# Revit family: RRHS
name_source: partatom
category: Generic Models
revit_build: Autodesk Revit 2018 (Build: 20190510_1515(x64)
units: mm (PartAtom-declared; Revit-internal decimal feet)

## family parameters
Always vertical = No
Can host rebar = No
Cut with Voids When Loaded = No
Part Type = Normal
Room Calculation Point = No
Round Connector Dimension = Use Diameter
Shared = Yes
Work Plane-Based = Yes

## types (7) — shared parameters
Default Elevation = 48 "
Spacer Material = <By Category>

## per-type parameters (varying)
| type | Description | Inside Diameter | Inside Radius | Length |
| RRHS5161 | Spacer Hygienic 304 5/16 Inch Hole Dia 1 Inch long | 0.313 " | 0.157 " | 1 " |
| RRHS5162 | Spacer Hygienic 304 5/16 Inch Hole Dia 2 Inch long | 0.313 " | 0.157 " | 2 " |
| RRHS5164 | Spacer Hygenic 304 5/16 Inch Hole Dia 4 Inch long | 0.313 " | 0.157 " | 4 " |
| RRHS7162 | Spacer Hygenic 304 7/16 Inch Hole Dia 2 Inch long | 0.438 " | 0.219 " | 2 " |
| RRHS7164 | Spacer Hygenic 304 7/16 Inch Hole Dia 4 Inch long | 0.438 " | 0.219 " | 4 " |
| RRHS7161 | Spacer Hygenic 304 7/16 Inch Hole Dia 1 Inch long | 0.438 " | 0.219 " | 1 " |
| RRHS9162 | Spacer Hygienic 304 9/16 Inch Hole Dia 2 Inch long | 0.563 " | 0.282 " | 2 " |

note: column(s) folded — value = type name in every type: Catalog Number

## geometry (parser evidence)
native form markers: Sweep x4
no freeform markers — native parametric forms only
